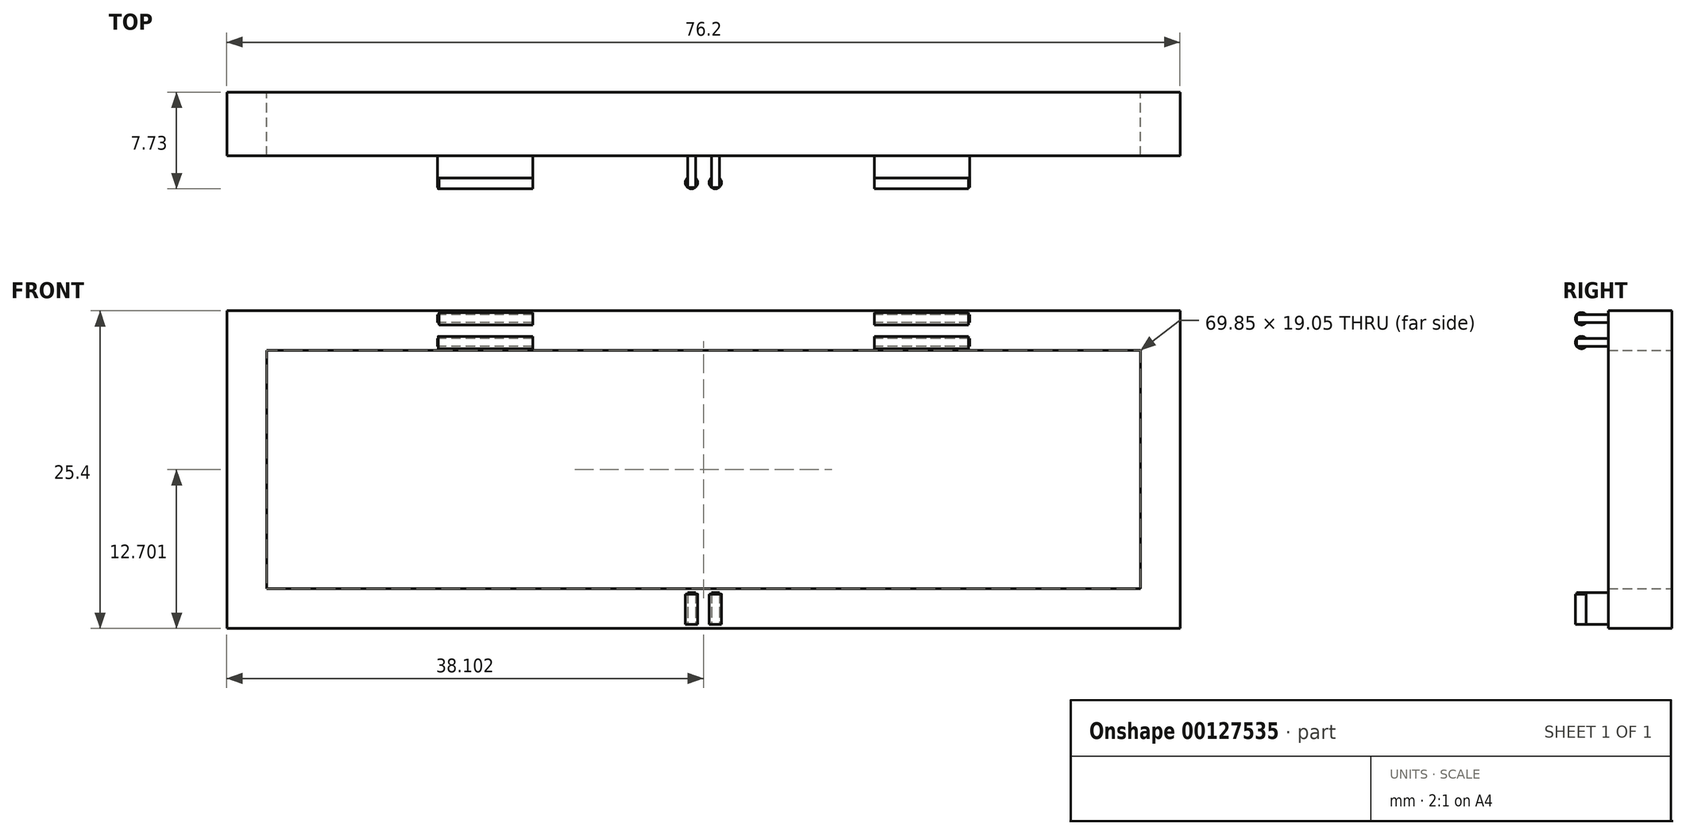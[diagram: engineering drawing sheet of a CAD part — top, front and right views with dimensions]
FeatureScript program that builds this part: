
annotation { "Feature Type Name" : "Feature", "Feature Type Description" : "" }
export const myFeature = defineFeature(function(context is Context, id is Id, definition is map)
    precondition{}
    {
        {
            var Q0;
            Q0=qCreatedBy(makeId("Front.planeOp"),FACE);
            var sketch = newSketch(context, id + "F0", { "sketchPlane" : qUnion([Q0])});
            skLineSegment(sketch, "E0.bottom", {"start": v(-29.34, 18.1) * mm, "end": v(46.86, 18.1) * mm});
            skLineSegment(sketch, "E0.top", {"start": v(-29.34, -7.3) * mm, "end": v(46.86, -7.3) * mm});
            skLineSegment(sketch, "E0.left", {"start": v(-29.34, 18.1) * mm, "end": v(-29.34, -7.3) * mm});
            skLineSegment(sketch, "E0.right", {"start": v(46.86, 18.1) * mm, "end": v(46.86, -7.3) * mm});
            skLineSegment(sketch, "E1.bottom", {"start": v(43.69, -4.12) * mm, "end": v(-26.16, -4.12) * mm});
            skLineSegment(sketch, "E1.top", {"start": v(43.69, 14.93) * mm, "end": v(-26.16, 14.93) * mm});
            skLineSegment(sketch, "E1.left", {"start": v(43.69, -4.12) * mm, "end": v(43.69, 14.93) * mm});
            skLineSegment(sketch, "E1.right", {"start": v(-26.16, -4.12) * mm, "end": v(-26.16, 14.93) * mm});
            skPoint(sketch, "E1.middle", {"position": v(8.76, 5.4) * mm});
            skPoint(sketch, "E1.middle.positionSnap0", {"position": v(46.86, 5.4) * mm});
            skPoint(sketch, "E1.middle.positionSnap1", {"position": v(8.76, 18.1) * mm});
            skPoint(sketch, "E1.centerSnap0", {"position": v(46.86, 5.4) * mm});
            skPoint(sketch, "E1.centerSnap1", {"position": v(8.76, 18.1) * mm});
            skSolve(sketch);
        }
        {
            var Q0;
            Q0 = qSketchRegion(id + "F0", true);
            extrude(context, id + "F1", {"entities" : qUnion([Q0]), "depth" : 5.08 * mm});
        }
        {
            var Q0;
            Q0=makeQuery(id+"F1.opExtrude","CAP_FACE",FACE,{"disambiguationData":[OSD([sQuery(id+"F0.wireOp",EDGE,"E0.bottom"),sQuery(id+"F0.wireOp",EDGE,"E0.top"),sQuery(id+"F0.wireOp",EDGE,"E0.left"),sQuery(id+"F0.wireOp",EDGE,"E0.right"),sQuery(id+"F0.wireOp",EDGE,"E1.bottom"),sQuery(id+"F0.wireOp",EDGE,"E1.top"),sQuery(id+"F0.wireOp",EDGE,"E1.left"),sQuery(id+"F0.wireOp",EDGE,"E1.right")])],"isStart":false});
            var sketch = newSketch(context, id + "F2", { "sketchPlane" : qUnion([Q0])});
            skLineSegment(sketch, "E2", {"start": v(43.69, 14.93) * mm, "end": v(43.69, 18.1) * mm});
            skLineSegment(sketch, "E3", {"start": v(8.76, 21.14) * mm, "end": v(43.69, 21.14) * mm});
            skPoint(sketch, "E3.startSnap0", {"position": v(8.76, 18.1) * mm});
            skLineSegment(sketch, "E4.bottom", {"start": v(30.03, 17.78) * mm, "end": v(22.41, 17.78) * mm});
            skLineSegment(sketch, "E4.top", {"start": v(30.03, 15.24) * mm, "end": v(22.41, 15.24) * mm});
            skLineSegment(sketch, "E4.left", {"start": v(30.03, 17.78) * mm, "end": v(30.03, 15.24) * mm});
            skLineSegment(sketch, "E4.right", {"start": v(22.41, 17.78) * mm, "end": v(22.41, 15.24) * mm});
            skPoint(sketch, "E4.middle", {"position": v(26.22, 16.51) * mm});
            skPoint(sketch, "E4.middle.positionSnap0", {"position": v(43.69, 16.51) * mm});
            skPoint(sketch, "E4.middle.positionSnap1", {"position": v(26.22, 21.14) * mm});
            skPoint(sketch, "E4.centerSnap0", {"position": v(43.69, 16.51) * mm});
            skPoint(sketch, "E4.centerSnap1", {"position": v(26.22, 21.14) * mm});
            skLineSegment(sketch, "E5.bottom", {"start": v(30.03, 17.15) * mm, "end": v(22.41, 17.15) * mm});
            skLineSegment(sketch, "E5.top", {"start": v(30.03, 15.88) * mm, "end": v(22.41, 15.88) * mm});
            skLineSegment(sketch, "E5.left", {"start": v(30.03, 17.15) * mm, "end": v(30.03, 15.88) * mm});
            skLineSegment(sketch, "E5.right", {"start": v(22.41, 17.15) * mm, "end": v(22.41, 15.88) * mm});
            skLineSegment(sketch, "E6", {"start": v(8.76, 21.14) * mm, "end": v(-26.16, 21.14) * mm});
            skLineSegment(sketch, "E7.bottom", {"start": v(-4.9, 17.78) * mm, "end": v(-12.51, 17.78) * mm});
            skLineSegment(sketch, "E7.top", {"start": v(-4.9, 15.24) * mm, "end": v(-12.51, 15.24) * mm});
            skLineSegment(sketch, "E7.left", {"start": v(-4.9, 17.78) * mm, "end": v(-4.9, 15.24) * mm});
            skLineSegment(sketch, "E7.right", {"start": v(-12.51, 17.78) * mm, "end": v(-12.51, 15.24) * mm});
            skPoint(sketch, "E7.middle", {"position": v(-8.7, 16.51) * mm});
            skPoint(sketch, "E7.middle.positionSnap0", {"position": v(-8.7, 21.14) * mm});
            skPoint(sketch, "E7.middle.positionSnap1", {"position": v(22.41, 16.51) * mm});
            skPoint(sketch, "E7.centerSnap0", {"position": v(-8.7, 21.14) * mm});
            skPoint(sketch, "E7.centerSnap1", {"position": v(22.41, 16.51) * mm});
            skLineSegment(sketch, "E8.bottom", {"start": v(-4.9, 17.15) * mm, "end": v(-12.51, 17.15) * mm});
            skLineSegment(sketch, "E8.top", {"start": v(-4.9, 15.88) * mm, "end": v(-12.51, 15.88) * mm});
            skLineSegment(sketch, "E8.left", {"start": v(-4.9, 17.15) * mm, "end": v(-4.9, 15.88) * mm});
            skLineSegment(sketch, "E8.right", {"start": v(-12.51, 17.15) * mm, "end": v(-12.51, 15.88) * mm});
            skSolve(sketch);
        }
        {
            var Q0;
            {var subQ0=sQuery(id+"F2.wireOp",EDGE,"E4.bottom");Q0=makeQuery(id+"F2.imprint","IMPRINT",FACE,{"disambiguationData":[TD([[makeQuery(id+"F2.imprint","IMPRINT",EDGE,{"derivedFrom":subQ0}),1.0]])]});}
            var Q1;
            {var subQ0=sQuery(id+"F2.wireOp",EDGE,"E4.top");Q1=makeQuery(id+"F2.imprint","IMPRINT",FACE,{"disambiguationData":[TD([[makeQuery(id+"F2.imprint","IMPRINT",EDGE,{"derivedFrom":subQ0}),-1.0]])]});}
            var Q2;
            {var subQ0=sQuery(id+"F2.wireOp",EDGE,"E7.bottom");Q2=makeQuery(id+"F2.imprint","IMPRINT",FACE,{"disambiguationData":[TD([[makeQuery(id+"F2.imprint","IMPRINT",EDGE,{"derivedFrom":subQ0}),1.0]])]});}
            var Q3;
            {var subQ0=sQuery(id+"F2.wireOp",EDGE,"E7.top");Q3=makeQuery(id+"F2.imprint","IMPRINT",FACE,{"disambiguationData":[TD([[makeQuery(id+"F2.imprint","IMPRINT",EDGE,{"derivedFrom":subQ0}),-1.0]])]});}
            extrude(context, id + "F3", {"entities" : qUnion([Q0, Q1, Q2, Q3]), "operationType" : NewBodyOperationType.ADD, "depth" : 1.78 * mm});
        }
        {
            var Q0;
            Q0=makeQuery(id+"F1.opExtrude","CAP_FACE",FACE,{"disambiguationData":[OSD([sQuery(id+"F0.wireOp",EDGE,"E0.bottom"),sQuery(id+"F0.wireOp",EDGE,"E0.top"),sQuery(id+"F0.wireOp",EDGE,"E0.left"),sQuery(id+"F0.wireOp",EDGE,"E0.right"),sQuery(id+"F0.wireOp",EDGE,"E1.bottom"),sQuery(id+"F0.wireOp",EDGE,"E1.top"),sQuery(id+"F0.wireOp",EDGE,"E1.left"),sQuery(id+"F0.wireOp",EDGE,"E1.right")])],"isStart":false});
            var sketch = newSketch(context, id + "F4", { "sketchPlane" : qUnion([Q0])});
            skLineSegment(sketch, "E9", {"start": v(-26.16, -4.12) * mm, "end": v(-26.16, -7.3) * mm});
            skLineSegment(sketch, "E10.bottom", {"start": v(10.03, -4.44) * mm, "end": v(7.5, -4.44) * mm});
            skLineSegment(sketch, "E10.top", {"start": v(10.03, -6.98) * mm, "end": v(7.5, -6.98) * mm});
            skLineSegment(sketch, "E10.left", {"start": v(10.03, -4.44) * mm, "end": v(10.03, -6.98) * mm});
            skLineSegment(sketch, "E10.right", {"start": v(7.5, -4.44) * mm, "end": v(7.5, -6.98) * mm});
            skPoint(sketch, "E10.middle", {"position": v(8.76, -5.71) * mm});
            skPoint(sketch, "E10.middle.positionSnap0", {"position": v(8.76, -7.3) * mm});
            skPoint(sketch, "E10.middle.positionSnap1", {"position": v(-26.16, -5.71) * mm});
            skPoint(sketch, "E10.centerSnap0", {"position": v(8.76, -7.3) * mm});
            skPoint(sketch, "E10.centerSnap1", {"position": v(-26.16, -5.71) * mm});
            skLineSegment(sketch, "E11.bottom", {"start": v(9.4, -4.44) * mm, "end": v(8.13, -4.44) * mm});
            skLineSegment(sketch, "E11.top", {"start": v(9.4, -6.98) * mm, "end": v(8.13, -6.98) * mm});
            skLineSegment(sketch, "E11.left", {"start": v(9.4, -4.44) * mm, "end": v(9.4, -6.98) * mm});
            skLineSegment(sketch, "E11.right", {"start": v(8.13, -4.44) * mm, "end": v(8.13, -6.98) * mm});
            skSolve(sketch);
        }
        {
            var Q0;
            {var subQ0=sQuery(id+"F4.wireOp",EDGE,"E10.left");Q0=makeQuery(id+"F4.imprint","IMPRINT",FACE,{"disambiguationData":[TD([[makeQuery(id+"F4.imprint","IMPRINT",EDGE,{"derivedFrom":subQ0}),-1.0]])]});}
            var Q1;
            {var subQ0=sQuery(id+"F4.wireOp",EDGE,"E10.right");Q1=makeQuery(id+"F4.imprint","IMPRINT",FACE,{"disambiguationData":[TD([[makeQuery(id+"F4.imprint","IMPRINT",EDGE,{"derivedFrom":subQ0}),1.0]])]});}
            extrude(context, id + "F5", {"entities" : qUnion([Q0, Q1]), "operationType" : NewBodyOperationType.ADD, "depth" : 1.78 * mm});
        }
        {
            var Q0;
            Q0=makeQuery(id+"F3.opExtrude","CAP_FACE",FACE,{"disambiguationData":[OSD([sQuery(id+"F2.wireOp",EDGE,"E7.bottom"),sQuery(id+"F2.wireOp",EDGE,"E7.left"),sQuery(id+"F2.wireOp",EDGE,"E7.right"),sQuery(id+"F2.wireOp",EDGE,"E8.bottom")])],"isStart":false});
            var sketch = newSketch(context, id + "F6", { "sketchPlane" : qUnion([Q0])});
            skLineSegment(sketch, "E12.bottom", {"start": v(-12.51, 17.15) * mm, "end": v(-12.37, 17.15) * mm});
            skLineSegment(sketch, "E12.top", {"start": v(-12.51, 17.78) * mm, "end": v(-12.37, 17.78) * mm});
            skLineSegment(sketch, "E12.left", {"start": v(-12.51, 17.15) * mm, "end": v(-12.51, 17.78) * mm});
            skLineSegment(sketch, "E12.right", {"start": v(-12.37, 17.15) * mm, "end": v(-12.37, 17.78) * mm});
            skSolve(sketch);
        }
        {
            var Q0;
            Q0 = qSketchRegion(id + "F6", true);
            extrude(context, id + "F7", {"entities" : qUnion([Q0]), "operationType" : NewBodyOperationType.ADD, "depth" : 0.76 * mm});
        }
        {
            var Q0;
            Q0=makeQuery(id+"F7.opExtrude","SWEPT_FACE",FACE,{"disambiguationData":[OSD([sQuery(id+"F6.wireOp",EDGE,"E12.right")])]});
            var sketch = newSketch(context, id + "F8", { "sketchPlane" : qUnion([Q0])});
            skCircle(sketch, "E13", {"center": v(-7.24, 17.47) * mm, "radius": 0.5 * mm});
            skPoint(sketch, "E13.centerSnap0", {"position": v(-7.24, 17.15) * mm});
            skPoint(sketch, "E13.centerSnap1", {"position": v(-7.62, 17.47) * mm});
            skSolve(sketch);
        }
        {
            var Q0;
            Q0 = qSketchRegion(id + "F8", true);
            var Q1;
            {var subQ0=sQuery(id+"F2.wireOp",EDGE,"E7.left");Q1=makeQuery(id+"F3.opExtrude","SWEPT_FACE",FACE,{"disambiguationData":[OSD([subQ0]),TDD([makeQuery(id+"F2.imprint","IMPRINT",EDGE,{"disambiguationData":[TD([[makeQuery(id+"F2.imprint","INTERSECT",VERTEX,{"derivedFrom":[sQuery(id+"F2.wireOp",EDGE,"E7.bottom"),subQ0]}),-1.0]])],"derivedFrom":subQ0})])]});}
            extrude(context, id + "F9", {"entities" : qUnion([Q0]), "operationType" : NewBodyOperationType.ADD, "endBound" : BoundingType.UP_TO_SURFACE, "endBoundEntityFace" : qUnion([Q1]), "depth" : 25.4 * mm});
        }
        {
            var Q0;
            Q0=makeQuery(id+"F3.opExtrude","CAP_FACE",FACE,{"disambiguationData":[OSD([sQuery(id+"F2.wireOp",EDGE,"E7.top"),sQuery(id+"F2.wireOp",EDGE,"E7.left"),sQuery(id+"F2.wireOp",EDGE,"E7.right"),sQuery(id+"F2.wireOp",EDGE,"E8.top")])],"isStart":false});
            var sketch = newSketch(context, id + "F10", { "sketchPlane" : qUnion([Q0])});
            skLineSegment(sketch, "E14.bottom", {"start": v(-12.51, 15.24) * mm, "end": v(-12.44, 15.24) * mm});
            skLineSegment(sketch, "E14.top", {"start": v(-12.51, 15.88) * mm, "end": v(-12.44, 15.88) * mm});
            skLineSegment(sketch, "E14.left", {"start": v(-12.51, 15.24) * mm, "end": v(-12.51, 15.88) * mm});
            skLineSegment(sketch, "E14.right", {"start": v(-12.44, 15.24) * mm, "end": v(-12.44, 15.88) * mm});
            skSolve(sketch);
        }
        {
            var Q0;
            Q0 = qSketchRegion(id + "F10", true);
            extrude(context, id + "F11", {"entities" : qUnion([Q0]), "operationType" : NewBodyOperationType.ADD, "depth" : 0.76 * mm});
        }
        {
            var Q0;
            Q0=makeQuery(id+"F11.opExtrude","SWEPT_FACE",FACE,{"disambiguationData":[OSD([sQuery(id+"F10.wireOp",EDGE,"E14.right")])]});
            var sketch = newSketch(context, id + "F12", { "sketchPlane" : qUnion([Q0])});
            skCircle(sketch, "E15", {"center": v(-7.24, 15.56) * mm, "radius": 0.5 * mm});
            skPoint(sketch, "E15.centerSnap0", {"position": v(-7.62, 15.56) * mm});
            skPoint(sketch, "E15.centerSnap1", {"position": v(-7.24, 15.88) * mm});
            skSolve(sketch);
        }
        {
            var Q0;
            Q0 = qSketchRegion(id + "F12", true);
            var Q1;
            {var subQ0=sQuery(id+"F2.wireOp",EDGE,"E7.left");Q1=makeQuery(id+"F3.opExtrude","SWEPT_FACE",FACE,{"disambiguationData":[OSD([subQ0]),TDD([makeQuery(id+"F2.imprint","IMPRINT",EDGE,{"disambiguationData":[TD([[makeQuery(id+"F2.imprint","INTERSECT",VERTEX,{"derivedFrom":[sQuery(id+"F2.wireOp",EDGE,"E7.top"),subQ0]}),1.0]])],"derivedFrom":subQ0})])]});}
            extrude(context, id + "F13", {"entities" : qUnion([Q0]), "operationType" : NewBodyOperationType.ADD, "endBound" : BoundingType.UP_TO_SURFACE, "endBoundEntityFace" : qUnion([Q1]), "depth" : 25.4 * mm});
        }
        {
            var Q0;
            Q0=makeQuery(id+"F3.opExtrude","CAP_FACE",FACE,{"disambiguationData":[OSD([sQuery(id+"F2.wireOp",EDGE,"E4.bottom"),sQuery(id+"F2.wireOp",EDGE,"E4.left"),sQuery(id+"F2.wireOp",EDGE,"E4.right"),sQuery(id+"F2.wireOp",EDGE,"E5.bottom")])],"isStart":false});
            var sketch = newSketch(context, id + "F14", { "sketchPlane" : qUnion([Q0])});
            skLineSegment(sketch, "E16.bottom", {"start": v(30.03, 17.78) * mm, "end": v(29.94, 17.78) * mm});
            skLineSegment(sketch, "E16.top", {"start": v(30.03, 17.15) * mm, "end": v(29.94, 17.15) * mm});
            skLineSegment(sketch, "E16.left", {"start": v(30.03, 17.78) * mm, "end": v(30.03, 17.15) * mm});
            skLineSegment(sketch, "E16.right", {"start": v(29.94, 17.78) * mm, "end": v(29.94, 17.15) * mm});
            skSolve(sketch);
        }
        {
            var Q0;
            Q0 = qSketchRegion(id + "F14", true);
            extrude(context, id + "F15", {"entities" : qUnion([Q0]), "operationType" : NewBodyOperationType.ADD, "depth" : 0.76 * mm});
        }
        {
            var Q0;
            Q0=makeQuery(id+"F15.opExtrude","SWEPT_FACE",FACE,{"disambiguationData":[OSD([sQuery(id+"F14.wireOp",EDGE,"E16.right")])]});
            var sketch = newSketch(context, id + "F16", { "sketchPlane" : qUnion([Q0])});
            skCircle(sketch, "E17", {"center": v(7.24, 17.47) * mm, "radius": 0.5 * mm});
            skPoint(sketch, "E17.centerSnap0", {"position": v(7.24, 17.78) * mm});
            skPoint(sketch, "E17.centerSnap1", {"position": v(6.86, 17.47) * mm});
            skSolve(sketch);
        }
        {
            var Q0;
            Q0 = qSketchRegion(id + "F16", true);
            var Q1;
            {var subQ0=sQuery(id+"F2.wireOp",EDGE,"E4.right");Q1=makeQuery(id+"F3.opExtrude","SWEPT_FACE",FACE,{"disambiguationData":[OSD([subQ0]),TDD([makeQuery(id+"F2.imprint","IMPRINT",EDGE,{"disambiguationData":[TD([[makeQuery(id+"F2.imprint","INTERSECT",VERTEX,{"derivedFrom":[sQuery(id+"F2.wireOp",EDGE,"E4.bottom"),subQ0]}),-1.0]])],"derivedFrom":subQ0})])]});}
            extrude(context, id + "F17", {"entities" : qUnion([Q0]), "operationType" : NewBodyOperationType.ADD, "endBound" : BoundingType.UP_TO_SURFACE, "endBoundEntityFace" : qUnion([Q1]), "depth" : 25.4 * mm});
        }
        {
            var Q0;
            Q0=makeQuery(id+"F3.opExtrude","CAP_FACE",FACE,{"disambiguationData":[OSD([sQuery(id+"F2.wireOp",EDGE,"E4.top"),sQuery(id+"F2.wireOp",EDGE,"E4.left"),sQuery(id+"F2.wireOp",EDGE,"E4.right"),sQuery(id+"F2.wireOp",EDGE,"E5.top")])],"isStart":false});
            var sketch = newSketch(context, id + "F18", { "sketchPlane" : qUnion([Q0])});
            skLineSegment(sketch, "E18.bottom", {"start": v(30.03, 15.88) * mm, "end": v(29.96, 15.88) * mm});
            skLineSegment(sketch, "E18.top", {"start": v(30.03, 15.24) * mm, "end": v(29.96, 15.24) * mm});
            skLineSegment(sketch, "E18.left", {"start": v(30.03, 15.88) * mm, "end": v(30.03, 15.24) * mm});
            skLineSegment(sketch, "E18.right", {"start": v(29.96, 15.88) * mm, "end": v(29.96, 15.24) * mm});
            skSolve(sketch);
        }
        {
            var Q0;
            Q0 = qSketchRegion(id + "F18", true);
            extrude(context, id + "F19", {"entities" : qUnion([Q0]), "operationType" : NewBodyOperationType.ADD, "depth" : 0.76 * mm});
        }
        {
            var Q0;
            Q0=makeQuery(id+"F19.opExtrude","SWEPT_FACE",FACE,{"disambiguationData":[OSD([sQuery(id+"F18.wireOp",EDGE,"E18.right")])]});
            var sketch = newSketch(context, id + "F20", { "sketchPlane" : qUnion([Q0])});
            skCircle(sketch, "E19", {"center": v(7.24, 15.56) * mm, "radius": 0.5 * mm});
            skPoint(sketch, "E19.centerSnap0", {"position": v(7.62, 15.56) * mm});
            skPoint(sketch, "E19.centerSnap1", {"position": v(7.24, 15.88) * mm});
            skSolve(sketch);
        }
        {
            var Q0;
            Q0 = qSketchRegion(id + "F20", true);
            var Q1;
            {var subQ0=sQuery(id+"F2.wireOp",EDGE,"E4.right");Q1=makeQuery(id+"F3.opExtrude","SWEPT_FACE",FACE,{"disambiguationData":[OSD([subQ0]),TDD([makeQuery(id+"F2.imprint","IMPRINT",EDGE,{"disambiguationData":[TD([[makeQuery(id+"F2.imprint","INTERSECT",VERTEX,{"derivedFrom":[sQuery(id+"F2.wireOp",EDGE,"E4.top"),subQ0]}),1.0]])],"derivedFrom":subQ0})])]});}
            extrude(context, id + "F21", {"entities" : qUnion([Q0]), "operationType" : NewBodyOperationType.ADD, "endBound" : BoundingType.UP_TO_SURFACE, "endBoundEntityFace" : qUnion([Q1]), "depth" : 25.4 * mm});
        }
        {
            var Q0;
            Q0=makeQuery(id+"F5.opExtrude","CAP_FACE",FACE,{"disambiguationData":[OSD([sQuery(id+"F4.wireOp",EDGE,"E10.bottom"),sQuery(id+"F4.wireOp",EDGE,"E10.top"),sQuery(id+"F4.wireOp",EDGE,"E10.right"),sQuery(id+"F4.wireOp",EDGE,"E11.right")])],"isStart":false});
            var sketch = newSketch(context, id + "F22", { "sketchPlane" : qUnion([Q0])});
            skLineSegment(sketch, "E20.bottom", {"start": v(7.5, -4.44) * mm, "end": v(8.13, -4.44) * mm});
            skLineSegment(sketch, "E20.top", {"start": v(7.5, -4.56) * mm, "end": v(8.13, -4.56) * mm});
            skLineSegment(sketch, "E20.left", {"start": v(7.5, -4.44) * mm, "end": v(7.5, -4.56) * mm});
            skLineSegment(sketch, "E20.right", {"start": v(8.13, -4.44) * mm, "end": v(8.13, -4.56) * mm});
            skSolve(sketch);
        }
        {
            var Q0;
            Q0 = qSketchRegion(id + "F22", true);
            extrude(context, id + "F23", {"entities" : qUnion([Q0]), "operationType" : NewBodyOperationType.ADD, "depth" : 0.76 * mm});
        }
        {
            var Q0;
            Q0=makeQuery(id+"F23.opExtrude","SWEPT_FACE",FACE,{"disambiguationData":[OSD([sQuery(id+"F22.wireOp",EDGE,"E20.top")])]});
            var sketch = newSketch(context, id + "F24", { "sketchPlane" : qUnion([Q0])});
            skCircle(sketch, "E21", {"center": v(7.8, 7.24) * mm, "radius": 0.5 * mm});
            skPoint(sketch, "E21.centerSnap0", {"position": v(8.13, 7.24) * mm});
            skPoint(sketch, "E21.centerSnap1", {"position": v(7.8, 7.62) * mm});
            skSolve(sketch);
        }
        {
            var Q0;
            Q0 = qSketchRegion(id + "F24", true);
            var Q1;
            {var subQ0=sQuery(id+"F4.wireOp",EDGE,"E10.top");Q1=makeQuery(id+"F5.opExtrude","SWEPT_FACE",FACE,{"disambiguationData":[OSD([subQ0]),TDD([makeQuery(id+"F4.imprint","IMPRINT",EDGE,{"disambiguationData":[TD([[makeQuery(id+"F4.imprint","INTERSECT",VERTEX,{"derivedFrom":[subQ0,sQuery(id+"F4.wireOp",EDGE,"E10.right")]}),1.0]])],"derivedFrom":subQ0})])]});}
            extrude(context, id + "F25", {"entities" : qUnion([Q0]), "operationType" : NewBodyOperationType.ADD, "endBound" : BoundingType.UP_TO_SURFACE, "endBoundEntityFace" : qUnion([Q1]), "depth" : 25.4 * mm});
        }
        {
            var Q0;
            Q0=makeQuery(id+"F5.opExtrude","CAP_FACE",FACE,{"disambiguationData":[OSD([sQuery(id+"F4.wireOp",EDGE,"E10.bottom"),sQuery(id+"F4.wireOp",EDGE,"E10.top"),sQuery(id+"F4.wireOp",EDGE,"E10.left"),sQuery(id+"F4.wireOp",EDGE,"E11.left")])],"isStart":false});
            var sketch = newSketch(context, id + "F26", { "sketchPlane" : qUnion([Q0])});
            skLineSegment(sketch, "E22.bottom", {"start": v(9.4, -4.44) * mm, "end": v(10.03, -4.44) * mm});
            skLineSegment(sketch, "E22.top", {"start": v(9.4, -4.55) * mm, "end": v(10.03, -4.55) * mm});
            skLineSegment(sketch, "E22.left", {"start": v(9.4, -4.44) * mm, "end": v(9.4, -4.55) * mm});
            skLineSegment(sketch, "E22.right", {"start": v(10.03, -4.44) * mm, "end": v(10.03, -4.55) * mm});
            skSolve(sketch);
        }
        {
            var Q0;
            Q0 = qSketchRegion(id + "F26", true);
            extrude(context, id + "F27", {"entities" : qUnion([Q0]), "operationType" : NewBodyOperationType.ADD, "depth" : 0.76 * mm});
        }
        {
            var Q0;
            Q0=makeQuery(id+"F27.opExtrude","SWEPT_FACE",FACE,{"disambiguationData":[OSD([sQuery(id+"F26.wireOp",EDGE,"E22.top")])]});
            var sketch = newSketch(context, id + "F28", { "sketchPlane" : qUnion([Q0])});
            skCircle(sketch, "E23", {"center": v(9.71, 7.24) * mm, "radius": 0.5 * mm});
            skPoint(sketch, "E23.centerSnap0", {"position": v(10.03, 7.24) * mm});
            skPoint(sketch, "E23.centerSnap1", {"position": v(9.71, 6.86) * mm});
            skSolve(sketch);
        }
        {
            var Q0;
            Q0 = qSketchRegion(id + "F28", true);
            var Q1;
            {var subQ0=sQuery(id+"F4.wireOp",EDGE,"E10.top");Q1=makeQuery(id+"F5.opExtrude","SWEPT_FACE",FACE,{"disambiguationData":[OSD([subQ0]),TDD([makeQuery(id+"F4.imprint","IMPRINT",EDGE,{"disambiguationData":[TD([[makeQuery(id+"F4.imprint","INTERSECT",VERTEX,{"derivedFrom":[subQ0,sQuery(id+"F4.wireOp",EDGE,"E10.left")]}),-1.0]])],"derivedFrom":subQ0})])]});}
            extrude(context, id + "F29", {"entities" : qUnion([Q0]), "operationType" : NewBodyOperationType.ADD, "endBound" : BoundingType.UP_TO_SURFACE, "endBoundEntityFace" : qUnion([Q1]), "depth" : 25.4 * mm});
        }
    });
